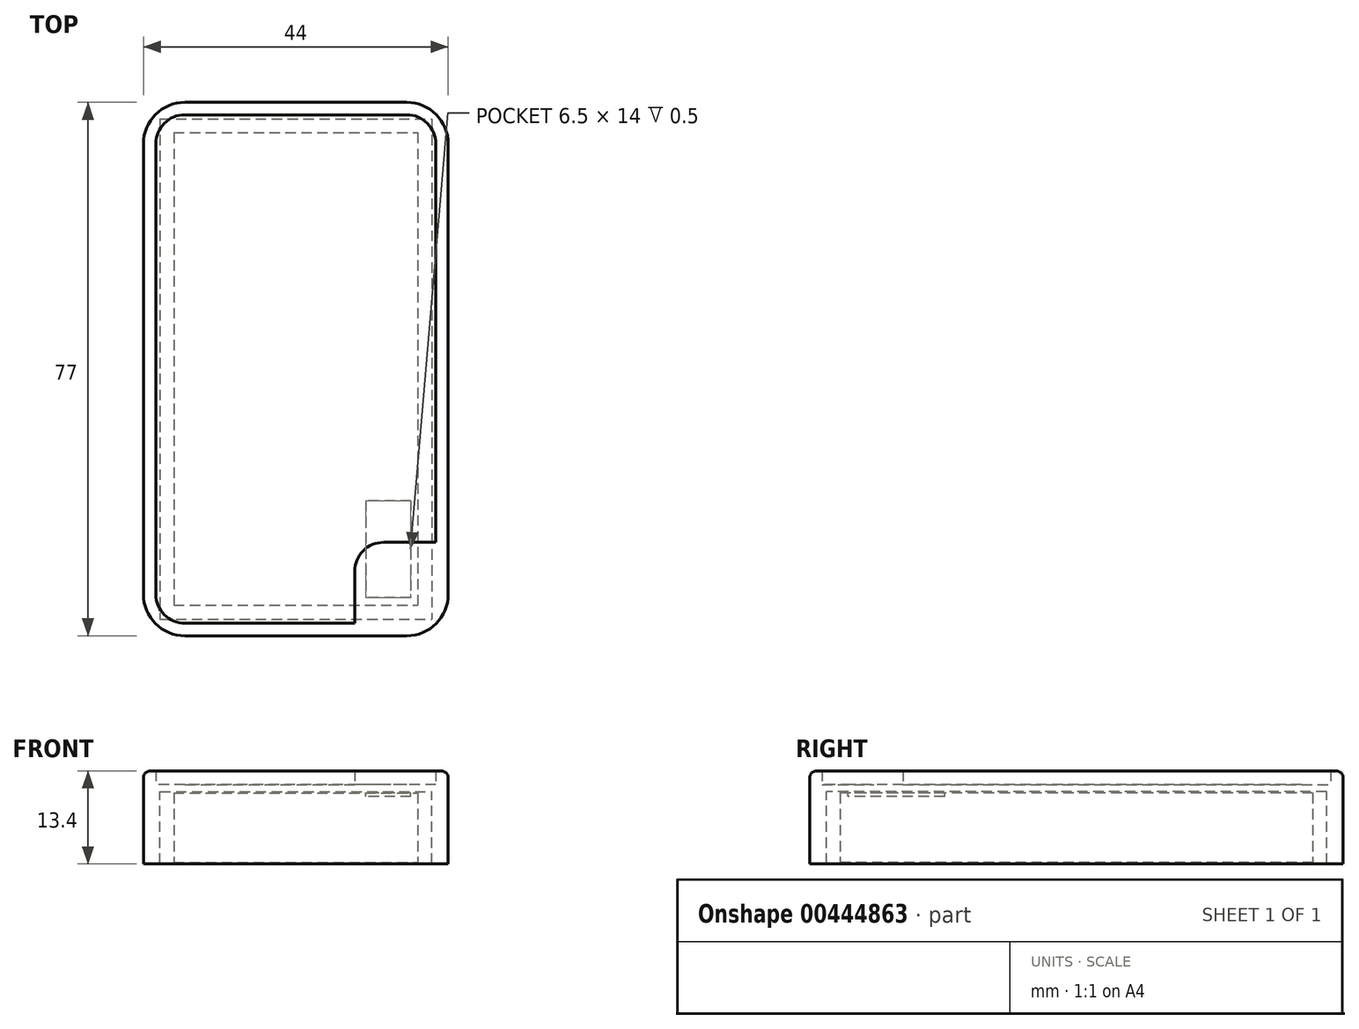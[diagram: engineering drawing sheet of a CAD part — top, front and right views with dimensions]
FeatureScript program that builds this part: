
annotation { "Feature Type Name" : "Feature", "Feature Type Description" : "" }
export const myFeature = defineFeature(function(context is Context, id is Id, definition is map)
    precondition{}
    {
        {
            var Q0;
            Q0=qCreatedBy(makeId("Top.planeOp"),FACE);
            var sketch = newSketch(context, id + "F0", { "sketchPlane" : qUnion([Q0])});
            skLineSegment(sketch, "E0.bottom", {"start": v(-17.6, 34.1) * mm, "end": v(17.6, 34.1) * mm});
            skLineSegment(sketch, "E0.top", {"start": v(-17.6, -34.1) * mm, "end": v(17.6, -34.1) * mm});
            skLineSegment(sketch, "E0.left", {"start": v(-17.6, 34.1) * mm, "end": v(-17.6, -34.1) * mm});
            skLineSegment(sketch, "E0.right", {"start": v(17.6, 34.1) * mm, "end": v(17.6, -34.1) * mm});
            skPoint(sketch, "E0.middle", {"position": v(0, 0) * mm});
            skSolve(sketch);
        }
        {
            var Q0;
            Q0=makeQuery(id+"F0.imprint","IMPRINT",FACE,{"disambiguationData":[TD([[makeQuery(id+"F0.imprint","IMPRINT",EDGE,{"derivedFrom":sQuery(id+"F0.wireOp",EDGE,"E0.bottom")}),-1.0]])]});
            extrude(context, id + "F1", {"entities" : qUnion([Q0]), "depth" : 10 * mm});
        }
        {
            var Q0;
            Q0=makeQuery(id+"F1.opExtrude","CAP_FACE",FACE,{"disambiguationData":[OSD([sQuery(id+"F0.wireOp",EDGE,"E0.bottom"),sQuery(id+"F0.wireOp",EDGE,"E0.top"),sQuery(id+"F0.wireOp",EDGE,"E0.left"),sQuery(id+"F0.wireOp",EDGE,"E0.right")])],"isStart":false});
            var sketch = newSketch(context, id + "F2", { "sketchPlane" : qUnion([Q0])});
            skLineSegment(sketch, "E1.bottom", {"start": v(16.6, -19) * mm, "end": v(10.1, -19) * mm});
            skLineSegment(sketch, "E1.top", {"start": v(16.6, -33) * mm, "end": v(10.1, -33) * mm});
            skLineSegment(sketch, "E1.left", {"start": v(16.6, -19) * mm, "end": v(16.6, -33) * mm});
            skLineSegment(sketch, "E1.right", {"start": v(10.1, -19) * mm, "end": v(10.1, -33) * mm});
            skPoint(sketch, "E1.middle", {"position": v(13.35, -26) * mm});
            skSolve(sketch);
        }
        {
            var Q0;
            Q0=qSketchRegion(id+"F2",true);
            extrude(context, id + "F3", {"entities" : qUnion([Q0]), "operationType" : NewBodyOperationType.REMOVE, "oppositeDirection" : true, "depth" : 0.5 * mm});
        }
        {
            var Q0;
            Q0=makeQuery(id+"F1.opExtrude","CAP_FACE",FACE,{"disambiguationData":[OSD([sQuery(id+"F0.wireOp",EDGE,"E0.bottom"),sQuery(id+"F0.wireOp",EDGE,"E0.top"),sQuery(id+"F0.wireOp",EDGE,"E0.left"),sQuery(id+"F0.wireOp",EDGE,"E0.right")])],"isStart":false});
            var sketch = newSketch(context, id + "F4", { "sketchPlane" : qUnion([Q0])});
            skLineSegment(sketch, "E2.bottom", {"start": v(-19.6, 36.1) * mm, "end": v(19.6, 36.1) * mm});
            skLineSegment(sketch, "E2.top", {"start": v(-19.6, -36.1) * mm, "end": v(19.6, -36.1) * mm});
            skLineSegment(sketch, "E2.left", {"start": v(-19.6, 36.1) * mm, "end": v(-19.6, -36.1) * mm});
            skLineSegment(sketch, "E2.right", {"start": v(19.6, 36.1) * mm, "end": v(19.6, -36.1) * mm});
            skPoint(sketch, "E2.middle", {"position": v(0, 0) * mm});
            skLineSegment(sketch, "E3.bottom", {"start": v(-22, 38.5) * mm, "end": v(22, 38.5) * mm});
            skLineSegment(sketch, "E3.top", {"start": v(-22, -38.5) * mm, "end": v(22, -38.5) * mm});
            skLineSegment(sketch, "E3.left", {"start": v(-22, 38.5) * mm, "end": v(-22, -38.5) * mm});
            skLineSegment(sketch, "E3.right", {"start": v(22, 38.5) * mm, "end": v(22, -38.5) * mm});
            skSolve(sketch);
        }
        {
            var Q0;
            Q0 = qSketchRegion(id + "F4", true);
            extrude(context, id + "F5", {"entities" : qUnion([Q0]), "oppositeDirection" : true, "depth" : 10.2 * mm, "hasSecondDirection" : true, "secondDirectionOppositeDirection" : false, "secondDirectionDepth" : 0.2 * mm});
        }
        {
            var Q0;
            Q0=makeQuery(id+"F5.opExtrude","SWEPT_EDGE",EDGE,{"disambiguationData":[OSD([sQuery(id+"F4.wireOp",EDGE,"E3.bottom"),sQuery(id+"F4.wireOp",EDGE,"E3.left")])]});
            var Q1;
            Q1=makeQuery(id+"F5.opExtrude","SWEPT_EDGE",EDGE,{"disambiguationData":[OSD([sQuery(id+"F4.wireOp",EDGE,"E3.bottom"),sQuery(id+"F4.wireOp",EDGE,"E3.right")])]});
            var Q2;
            Q2=makeQuery(id+"F5.opExtrude","SWEPT_EDGE",EDGE,{"disambiguationData":[OSD([sQuery(id+"F4.wireOp",EDGE,"E3.top"),sQuery(id+"F4.wireOp",EDGE,"E3.right")])]});
            var Q3;
            Q3=makeQuery(id+"F5.opExtrude","SWEPT_EDGE",EDGE,{"disambiguationData":[OSD([sQuery(id+"F4.wireOp",EDGE,"E3.top"),sQuery(id+"F4.wireOp",EDGE,"E3.left")])]});
            fillet(context, id + "F6", {"entities" : qUnion([Q0, Q1, Q2, Q3]), "radius" : 6 * mm, "tangentPropagation" : true, "allowEdgeOverflow" : false});
        }
        {
            var Q0;
            Q0=makeQuery(id+"F5.opExtrude","CAP_FACE",FACE,{"disambiguationData":[OSD([sQuery(id+"F4.wireOp",EDGE,"E2.bottom"),sQuery(id+"F4.wireOp",EDGE,"E2.top"),sQuery(id+"F4.wireOp",EDGE,"E2.left"),sQuery(id+"F4.wireOp",EDGE,"E2.right"),sQuery(id+"F4.wireOp",EDGE,"E3.bottom"),sQuery(id+"F4.wireOp",EDGE,"E3.top"),sQuery(id+"F4.wireOp",EDGE,"E3.left"),sQuery(id+"F4.wireOp",EDGE,"E3.right")])],"isStart":true});
            var sketch = newSketch(context, id + "F7", { "sketchPlane" : qUnion([Q0])});
            skLineSegment(sketch, "E4.0.0", {"start": v(-22, 32.5) * mm, "end": v(-22, -32.5) * mm});
            skArc(sketch, "E4.0.1", {"start": v(-22, -32.5) * mm, "mid": v(-20.24, -36.74) * mm, "end": v(-16, -38.5) * mm});
            skLineSegment(sketch, "E4.0.2", {"start": v(-16, -38.5) * mm, "end": v(16, -38.5) * mm});
            skArc(sketch, "E4.0.3", {"start": v(16, -38.5) * mm, "mid": v(20.24, -36.74) * mm, "end": v(22, -32.5) * mm});
            skLineSegment(sketch, "E4.0.4", {"start": v(22, -32.5) * mm, "end": v(22, 32.5) * mm});
            skArc(sketch, "E4.0.5", {"start": v(22, 32.5) * mm, "mid": v(20.24, 36.74) * mm, "end": v(16, 38.5) * mm});
            skLineSegment(sketch, "E4.0.6", {"start": v(16, 38.5) * mm, "end": v(-16, 38.5) * mm});
            skArc(sketch, "E4.0.7", {"start": v(-16, 38.5) * mm, "mid": v(-20.24, 36.74) * mm, "end": v(-22, 32.5) * mm});
            skSolve(sketch);
        }
        {
            var Q0;
            Q0 = qSketchRegion(id + "F7", true);
            extrude(context, id + "F8", {"entities" : qUnion([Q0]), "operationType" : NewBodyOperationType.ADD, "depth" : 3 * mm});
        }
        {
            var Q0;
            Q0=makeQuery(id+"F8.opExtrude","CAP_FACE",FACE,{"disambiguationData":[OSD([sQuery(id+"F7.wireOp",EDGE,"E4.0.0"),sQuery(id+"F7.wireOp",EDGE,"E4.0.1"),sQuery(id+"F7.wireOp",EDGE,"E4.0.2"),sQuery(id+"F7.wireOp",EDGE,"E4.0.3"),sQuery(id+"F7.wireOp",EDGE,"E4.0.4"),sQuery(id+"F7.wireOp",EDGE,"E4.0.5"),sQuery(id+"F7.wireOp",EDGE,"E4.0.6"),sQuery(id+"F7.wireOp",EDGE,"E4.0.7")])],"isStart":false});
            var sketch = newSketch(context, id + "F9", { "sketchPlane" : qUnion([Q0])});
            skLineSegment(sketch, "E5.0", {"start": v(16, 36.7) * mm, "end": v(-16, 36.7) * mm});
            skArc(sketch, "E5.1", {"start": v(20.2, 32.5) * mm, "mid": v(18.97, 35.47) * mm, "end": v(16, 36.7) * mm});
            skArc(sketch, "E5.2", {"start": v(-16, 36.7) * mm, "mid": v(-18.97, 35.47) * mm, "end": v(-20.2, 32.5) * mm});
            skLineSegment(sketch, "E5.3", {"start": v(20.2, -32.5) * mm, "end": v(20.2, 32.5) * mm});
            skLineSegment(sketch, "E5.4", {"start": v(-20.2, 32.5) * mm, "end": v(-20.2, -32.5) * mm});
            skArc(sketch, "E5.5", {"start": v(-20.2, -32.5) * mm, "mid": v(-18.97, -35.47) * mm, "end": v(-16, -36.7) * mm});
            skLineSegment(sketch, "E5.6", {"start": v(-16, -36.7) * mm, "end": v(16, -36.7) * mm});
            skArc(sketch, "E5.7", {"start": v(16, -36.7) * mm, "mid": v(18.97, -35.47) * mm, "end": v(20.2, -32.5) * mm});
            skSolve(sketch);
        }
        {
            var Q0;
            Q0 = qSketchRegion(id + "F9", true);
            extrude(context, id + "F10", {"entities" : qUnion([Q0]), "operationType" : NewBodyOperationType.REMOVE, "oppositeDirection" : true, "depth" : 2 * mm});
        }
        {
            var Q0;
            Q0=makeQuery(id+"F10.boolean.opBoolean","COPY",FACE,{"derivedFrom":makeQuery(id+"F10.opExtrude","CAP_FACE",FACE,{"disambiguationData":[OSD([sQuery(id+"F9.wireOp",EDGE,"E5.0"),sQuery(id+"F9.wireOp",EDGE,"E5.1"),sQuery(id+"F9.wireOp",EDGE,"E5.2"),sQuery(id+"F9.wireOp",EDGE,"E5.3"),sQuery(id+"F9.wireOp",EDGE,"E5.4"),sQuery(id+"F9.wireOp",EDGE,"E5.5"),sQuery(id+"F9.wireOp",EDGE,"E5.6"),sQuery(id+"F9.wireOp",EDGE,"E5.7")])],"isStart":false})});
            var sketch = newSketch(context, id + "F11", { "sketchPlane" : qUnion([Q0])});
            skLineSegment(sketch, "E6.bottom", {"start": v(23.5, -40) * mm, "end": v(8.5, -40) * mm});
            skLineSegment(sketch, "E6.top", {"start": v(23.5, -25) * mm, "end": v(12.7, -25) * mm});
            skLineSegment(sketch, "E6.left", {"start": v(23.5, -40) * mm, "end": v(23.5, -25) * mm});
            skLineSegment(sketch, "E6.right", {"start": v(8.5, -40) * mm, "end": v(8.5, -29.2) * mm});
            skPoint(sketch, "E6.middle", {"position": v(16, -32.5) * mm});
            skLineSegment(sketch, "E7.0.0", {"start": v(-16, -36.7) * mm, "end": v(16, -36.7) * mm});
            skArc(sketch, "E7.0.1", {"start": v(16, -36.7) * mm, "mid": v(18.97, -35.47) * mm, "end": v(20.2, -32.5) * mm});
            skLineSegment(sketch, "E7.0.2", {"start": v(20.2, -32.5) * mm, "end": v(20.2, 32.5) * mm});
            skArc(sketch, "E7.0.3", {"start": v(20.2, 32.5) * mm, "mid": v(18.97, 35.47) * mm, "end": v(16, 36.7) * mm});
            skLineSegment(sketch, "E7.0.4", {"start": v(16, 36.7) * mm, "end": v(-16, 36.7) * mm});
            skArc(sketch, "E7.0.5", {"start": v(-16, 36.7) * mm, "mid": v(-18.97, 35.47) * mm, "end": v(-20.2, 32.5) * mm});
            skLineSegment(sketch, "E7.0.6", {"start": v(-20.2, 32.5) * mm, "end": v(-20.2, -32.5) * mm});
            skArc(sketch, "E7.0.7", {"start": v(-20.2, -32.5) * mm, "mid": v(-18.97, -35.47) * mm, "end": v(-16, -36.7) * mm});
            skPoint(sketch, "E8.visualSharp", {"position": v(8.5, -25) * mm});
            skArc(sketch, "E8.filletArc", {"start": v(12.7, -25) * mm, "mid": v(9.73, -26.23) * mm, "end": v(8.5, -29.2) * mm});
            skSolve(sketch);
        }
        {
            var Q0;
            {var subQ0=sQuery(id+"F11.wireOp",EDGE,"E7.0.1");Q0=makeQuery(id+"F11.imprint","IMPRINT",FACE,{"disambiguationData":[TD([[makeQuery(id+"F11.imprint","IMPRINT",EDGE,{"derivedFrom":subQ0}),1.0]])]});}
            var Q1;
            Q1=makeQuery(id+"F8.opExtrude","CAP_FACE",FACE,{"disambiguationData":[OSD([sQuery(id+"F7.wireOp",EDGE,"E4.0.0"),sQuery(id+"F7.wireOp",EDGE,"E4.0.1"),sQuery(id+"F7.wireOp",EDGE,"E4.0.2"),sQuery(id+"F7.wireOp",EDGE,"E4.0.3"),sQuery(id+"F7.wireOp",EDGE,"E4.0.4"),sQuery(id+"F7.wireOp",EDGE,"E4.0.5"),sQuery(id+"F7.wireOp",EDGE,"E4.0.6"),sQuery(id+"F7.wireOp",EDGE,"E4.0.7")])],"isStart":false});
            extrude(context, id + "F12", {"entities" : qUnion([Q0]), "operationType" : NewBodyOperationType.ADD, "endBound" : BoundingType.UP_TO_SURFACE, "endBoundEntityFace" : qUnion([Q1]), "depth" : 25 * mm});
        }
        {
            var Q0;
            Q0=makeQuery(id+"F10.boolean.opBoolean","COPY",FACE,{"derivedFrom":makeQuery(id+"F10.opExtrude","CAP_FACE",FACE,{"disambiguationData":[OSD([sQuery(id+"F9.wireOp",EDGE,"E5.0"),sQuery(id+"F9.wireOp",EDGE,"E5.1"),sQuery(id+"F9.wireOp",EDGE,"E5.2"),sQuery(id+"F9.wireOp",EDGE,"E5.3"),sQuery(id+"F9.wireOp",EDGE,"E5.4"),sQuery(id+"F9.wireOp",EDGE,"E5.5"),sQuery(id+"F9.wireOp",EDGE,"E5.6"),sQuery(id+"F9.wireOp",EDGE,"E5.7")])],"isStart":false})});
            extrude(context, id + "F13", {"entities" : qUnion([Q0]), "depth" : 2 * mm});
        }
        {
            var Q0;
            Q0=makeQuery(id+"F8.opExtrude","CAP_EDGE",EDGE,{"disambiguationData":[OSD([sQuery(id+"F7.wireOp",EDGE,"E4.0.0")])],"isStart":false});
            fillet(context, id + "F14", {"entities" : qUnion([Q0]), "radius" : 1 * mm, "tangentPropagation" : true, "allowEdgeOverflow" : false});
        }
    });
